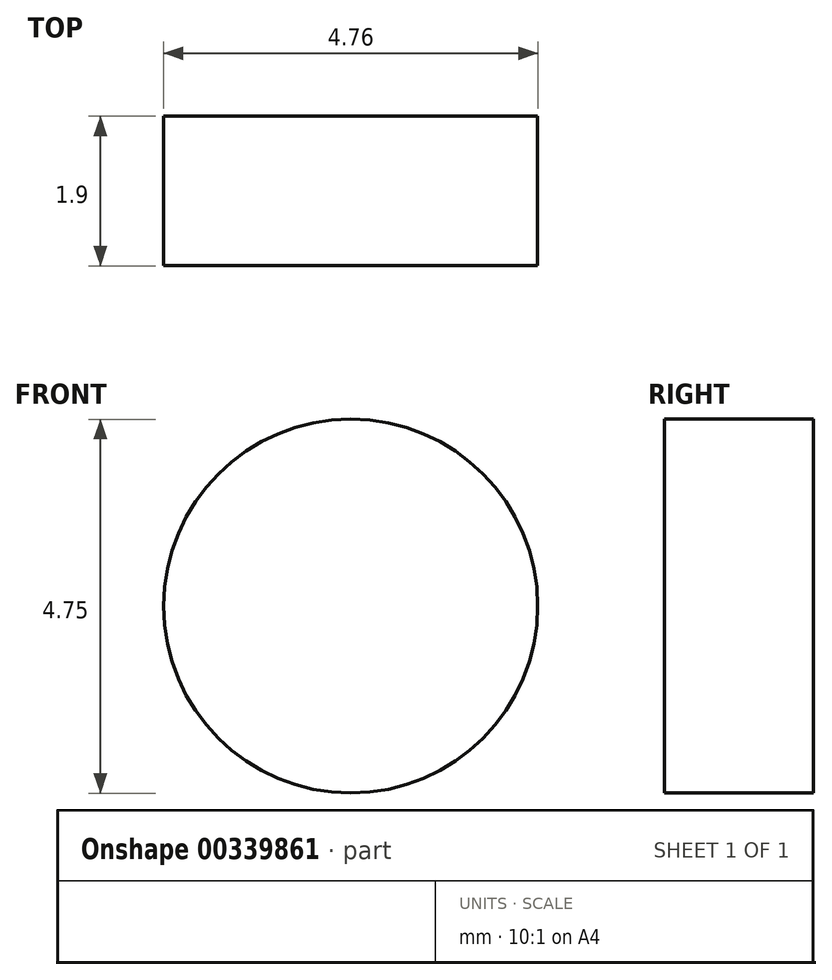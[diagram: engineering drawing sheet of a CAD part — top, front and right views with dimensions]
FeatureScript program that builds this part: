
annotation { "Feature Type Name" : "Feature", "Feature Type Description" : "" }
export const myFeature = defineFeature(function(context is Context, id is Id, definition is map)
    precondition{}
    {
        {
            var Q0;
            Q0=qCreatedBy(makeId("Front.planeOp"),FACE);
            var sketch = newSketch(context, id + "F0", { "sketchPlane" : qUnion([Q0])});
            skCircle(sketch, "E0.MirrorC", {"center": v(-4.12, 22.47) * mm, "radius": 2.38 * mm});
            skCircle(sketch, "E1.MirrorC", {"center": v(-4.12, 15.33) * mm, "radius": 1.6 * mm});
            skLineSegment(sketch, "E2", {"start": v(-7.3, 27.38) * mm, "end": v(-7.3, 15.33) * mm});
            skLineSegment(sketch, "E3", {"start": v(-4.12, 12.15) * mm, "end": v(0.67, 12.15) * mm});
            skPoint(sketch, "E4.center.orphan", {"position": v(27.63, 24.74) * mm});
            skPoint(sketch, "E5.visualSharp", {"position": v(-7.3, 12.15) * mm});
            skArc(sketch, "E5.filletArc", {"start": v(-7.3, 15.33) * mm, "mid": v(-6.37, 13.08) * mm, "end": v(-4.12, 12.15) * mm});
            skLineSegment(sketch, "E6", {"start": v(7.8, -2.13) * mm, "end": v(6.6, 15.17) * mm});
            skArc(sketch, "E7.filletArc", {"start": v(9.77, 18.57) * mm, "mid": v(7.45, 17.56) * mm, "end": v(6.6, 15.17) * mm});
            skArc(sketch, "E8.filletArc", {"start": v(7.8, -2.13) * mm, "mid": v(8.8, -4.23) * mm, "end": v(10.97, -5.08) * mm});
            skPoint(sketch, "E9.visualSharp", {"position": v(3.63, 12.15) * mm});
            skArc(sketch, "E9.filletArc", {"start": v(3.84, 9.2) * mm, "mid": v(2.83, 11.3) * mm, "end": v(0.67, 12.15) * mm});
            skArc(sketch, "E10.MirrorCS", {"start": v(19.67, 9.2) * mm, "mid": v(20.68, 11.3) * mm, "end": v(22.84, 12.15) * mm});
            skLineSegment(sketch, "E11.MirrorCS", {"start": v(27.63, 12.15) * mm, "end": v(22.84, 12.15) * mm});
            skArc(sketch, "E12.MirrorCS", {"start": v(30.8, 15.33) * mm, "mid": v(29.88, 13.08) * mm, "end": v(27.63, 12.15) * mm});
            skCircle(sketch, "E13.MirrorC", {"center": v(27.63, 15.33) * mm, "radius": 1.6 * mm});
            skCircle(sketch, "E14.MirrorC", {"center": v(27.63, 22.47) * mm, "radius": 2.38 * mm});
            skArc(sketch, "E15.MirrorCS", {"start": v(13.76, 18.57) * mm, "mid": v(16.08, 17.56) * mm, "end": v(16.92, 15.17) * mm});
            skArc(sketch, "E16.MirrorCS", {"start": v(15.72, -2.13) * mm, "mid": v(14.72, -4.23) * mm, "end": v(12.55, -5.08) * mm});
            skLineSegment(sketch, "E17", {"start": v(9.77, 18.57) * mm, "end": v(13.76, 18.57) * mm});
            skLineSegment(sketch, "E18", {"start": v(10.97, -5.08) * mm, "end": v(12.55, -5.08) * mm});
            skLineSegment(sketch, "E19", {"start": v(30.8, 27.38) * mm, "end": v(30.8, 15.33) * mm});
            skLineSegment(sketch, "E20", {"start": v(-7.3, 27.38) * mm, "end": v(30.8, 27.38) * mm});
            skLineSegment(sketch, "E21", {"start": v(16.92, 15.17) * mm, "end": v(15.72, -2.13) * mm});
            skLineSegment(sketch, "E22", {"start": v(3.84, 9.2) * mm, "end": v(5.05, -8.22) * mm});
            skLineSegment(sketch, "E23", {"start": v(5.05, -8.22) * mm, "end": v(18.46, -8.22) * mm});
            skLineSegment(sketch, "E24", {"start": v(19.67, 9.2) * mm, "end": v(18.46, -8.22) * mm});
            skPoint(sketch, "E25.end.orphan", {"position": v(0, -8.22) * mm});
            skSolve(sketch);
        }
        {
            var Q0;
            Q0=makeQuery(id+"F0.imprint","IMPRINT",FACE,{"disambiguationData":[TD([[makeQuery(id+"F0.imprint","IMPRINT",EDGE,{"derivedFrom":sQuery(id+"F0.wireOp",EDGE,"E0.MirrorC")}),1.0]])]});
            extrude(context, id + "F1", {"entities" : qUnion([Q0]), "depth" : 1.9 * mm});
        }
    });
